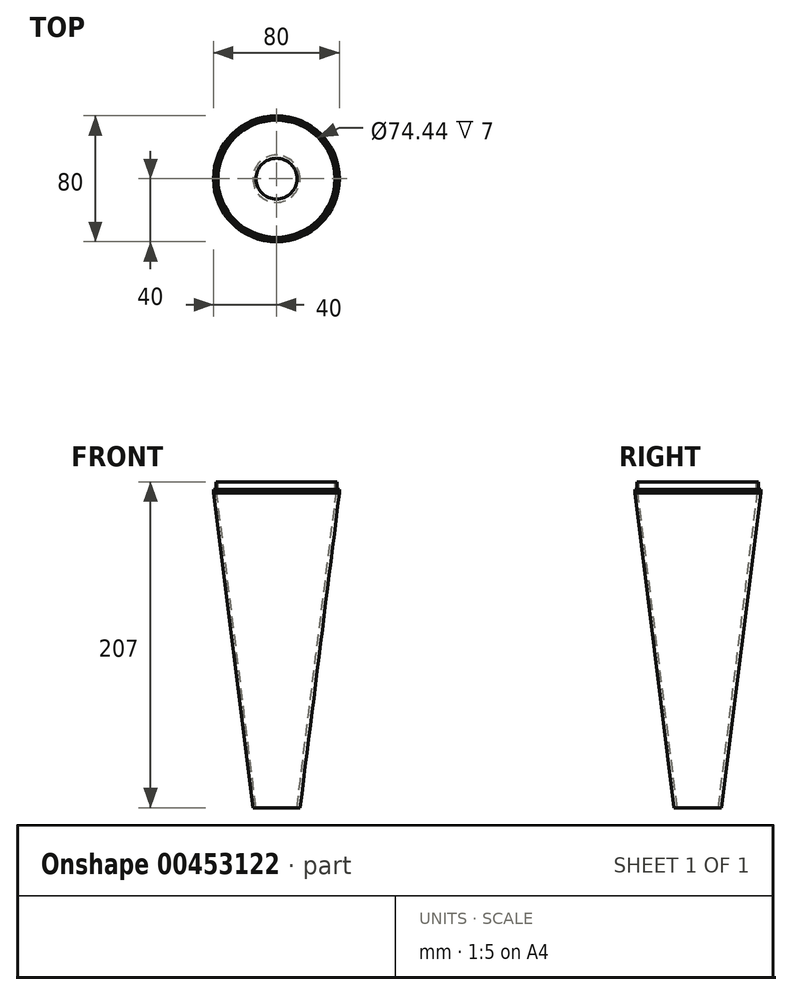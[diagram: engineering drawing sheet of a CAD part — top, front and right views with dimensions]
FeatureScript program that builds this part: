
annotation { "Feature Type Name" : "Feature", "Feature Type Description" : "" }
export const myFeature = defineFeature(function(context is Context, id is Id, definition is map)
    precondition{}
    {
        {
            var Q0;
            Q0=qCreatedBy(makeId("Top.planeOp"),FACE);
            var sketch = newSketch(context, id + "F0", { "sketchPlane" : qUnion([Q0])});
            skCircle(sketch, "E0", {"center": v(0, 0) * mm, "radius": 40 * mm});
            skSolve(sketch);
        }
        {
            var Q0;
            Q0=makeQuery(id+"F0.imprint","IMPRINT",FACE,{"disambiguationData":[TD([[makeQuery(id+"F0.imprint","IMPRINT",EDGE,{"derivedFrom":sQuery(id+"F0.wireOp",EDGE,"E0")}),1.0]])]});
            extrude(context, id + "F1", {"entities" : qUnion([Q0]), "depth" : 2 * mm});
        }
        {
            var Q0;
            Q0=makeQuery(id+"F1.opExtrude","CAP_FACE",FACE,{"disambiguationData":[OSD([sQuery(id+"F0.wireOp",EDGE,"E0")])],"isStart":false});
            var sketch = newSketch(context, id + "F2", { "sketchPlane" : qUnion([Q0])});
            skCircle(sketch, "E1", {"center": v(0, 0) * mm, "radius": 38.5 * mm});
            skSolve(sketch);
        }
        {
            var Q0;
            Q0=makeQuery(id+"F2.imprint","IMPRINT",FACE,{"disambiguationData":[TD([[makeQuery(id+"F2.imprint","IMPRINT",EDGE,{"derivedFrom":sQuery(id+"F2.wireOp",EDGE,"E1")}),1.0]])]});
            extrude(context, id + "F3", {"entities" : qUnion([Q0]), "operationType" : NewBodyOperationType.ADD, "depth" : 5 * mm});
        }
        {
            var Q0;
            Q0=makeQuery(id+"F1.opExtrude","CAP_FACE",FACE,{"disambiguationData":[OSD([sQuery(id+"F0.wireOp",EDGE,"E0")])],"isStart":true});
            var sketch = newSketch(context, id + "F4", { "sketchPlane" : qUnion([Q0])});
            skSolve(sketch);
        }
        {
            var Q0;
            Q0=qCreatedBy(makeId("Right.planeOp"),FACE);
            var sketch = newSketch(context, id + "F5", { "sketchPlane" : qUnion([Q0])});
            skLineSegment(sketch, "E2", {"start": v(-8.45, -200) * mm, "end": v(8.45, -200) * mm});
            skSolve(sketch);
        }
        {
            var Q0;
            Q0=sQuery(id+"F5.wireOp",VERTEX,"E2.start");
            var Q1;
            Q1=qCreatedBy(makeId("Top.planeOp"),FACE);
            cPlane(context, id + "F6", {"entities" : qUnion([Q0, Q1]), "cplaneType" : CPlaneType.PLANE_POINT, "offset" : 25 * mm, "flipAlignment" : true, "width" : 150 * mm, "height" : 150 * mm});
        }
        {
            var Q0;
            Q0=qCreatedBy(id+"F6.planeOp",FACE);
            var sketch = newSketch(context, id + "F7", { "sketchPlane" : qUnion([Q0])});
            skCircle(sketch, "E3", {"center": v(0, 0) * mm, "radius": 15 * mm});
            skSolve(sketch);
        }
        {
            var Q1;
            Q1=makeQuery(id+"F7.imprint","IMPRINT",FACE,{"disambiguationData":[TD([[makeQuery(id+"F7.imprint","IMPRINT",EDGE,{"derivedFrom":sQuery(id+"F7.wireOp",EDGE,"E3")}),1.0]])]});
            var Q2;
            Q2=makeQuery(id+"F4.imprint","IMPRINT",FACE,{"disambiguationData":[TD([[makeQuery(id+"F4.imprint","IMPRINT",EDGE,{"derivedFrom":makeQuery(id+"F1.opExtrude","CAP_EDGE",EDGE,{"disambiguationData":[OSD([sQuery(id+"F0.wireOp",EDGE,"E0")])],"isStart":true})}),-1.0]])]});
            loft(context, id + "F8", {"operationType" : NewBodyOperationType.ADD, "sheetProfilesArray" : [{ "sheetProfileEntities" : qUnion([Q1]) }, { "sheetProfileEntities" : qUnion([Q2]) }]});
        }
        {
            var Q0;
            Q0=makeQuery(id+"F8.opLoft","CAP_FACE",FACE,{"disambiguationData":[OSD([makeQuery(id+"F7.imprint","IMPRINT",FACE,{"disambiguationData":[TD([[makeQuery(id+"F7.imprint","IMPRINT",EDGE,{"derivedFrom":sQuery(id+"F7.wireOp",EDGE,"E3")}),1.0]])]})])],"isStart":true});
            shell(context, id + "F9", {"entities" : qUnion([Q0]), "thickness" : 2 * mm});
        }
        {
            var Q0;
            Q0=makeQuery(id+"F3.opExtrude","CAP_FACE",FACE,{"disambiguationData":[OSD([sQuery(id+"F2.wireOp",EDGE,"E1")])],"isStart":false});
            var sketch = newSketch(context, id + "F10", { "sketchPlane" : qUnion([Q0])});
            skCircle(sketch, "E4", {"center": v(0, 0) * mm, "radius": 37.22 * mm});
            skSolve(sketch);
        }
        {
            var Q0;
            Q0=makeQuery(id+"F10.imprint","IMPRINT",FACE,{"disambiguationData":[TD([[makeQuery(id+"F10.imprint","IMPRINT",EDGE,{"derivedFrom":sQuery(id+"F10.wireOp",EDGE,"E4")}),1.0]])]});
            extrude(context, id + "F11", {"entities" : qUnion([Q0]), "operationType" : NewBodyOperationType.REMOVE, "endBound" : BoundingType.UP_TO_NEXT, "oppositeDirection" : true, "depth" : 25 * mm});
        }
    });
